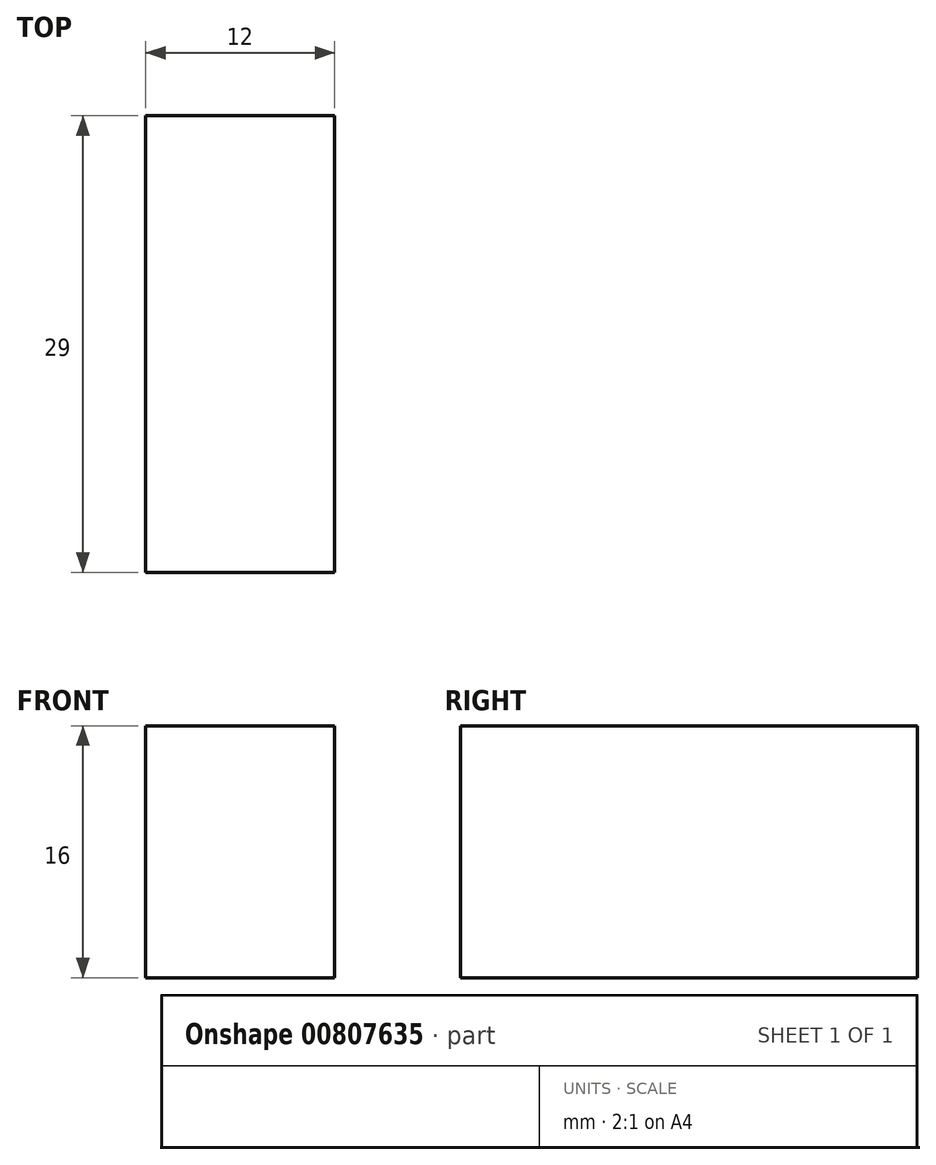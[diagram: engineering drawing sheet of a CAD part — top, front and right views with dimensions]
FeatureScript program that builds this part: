
annotation { "Feature Type Name" : "Feature", "Feature Type Description" : "" }
export const myFeature = defineFeature(function(context is Context, id is Id, definition is map)
    precondition{}
    {
        {
            var Q0;
            Q0=qCreatedBy(makeId("Top.planeOp"),FACE);
            var sketch = newSketch(context, id + "F0", { "sketchPlane" : qUnion([Q0])});
            skLineSegment(sketch, "E0.bottom", {"start": v(6, -14.5) * mm, "end": v(-6, -14.5) * mm});
            skLineSegment(sketch, "E0.top", {"start": v(6, 14.5) * mm, "end": v(-6, 14.5) * mm});
            skLineSegment(sketch, "E0.left", {"start": v(6, -14.5) * mm, "end": v(6, 14.5) * mm});
            skLineSegment(sketch, "E0.right", {"start": v(-6, -14.5) * mm, "end": v(-6, 14.5) * mm});
            skPoint(sketch, "E0.middle", {"position": v(0, 0) * mm});
            skSolve(sketch);
        }
        {
            var Q0;
            Q0 = qSketchRegion(id + "F0", true);
            extrude(context, id + "F1", {"entities" : qUnion([Q0]), "depth" : 16 * mm, "offsetDistance" : 25 * mm});
        }
    });
